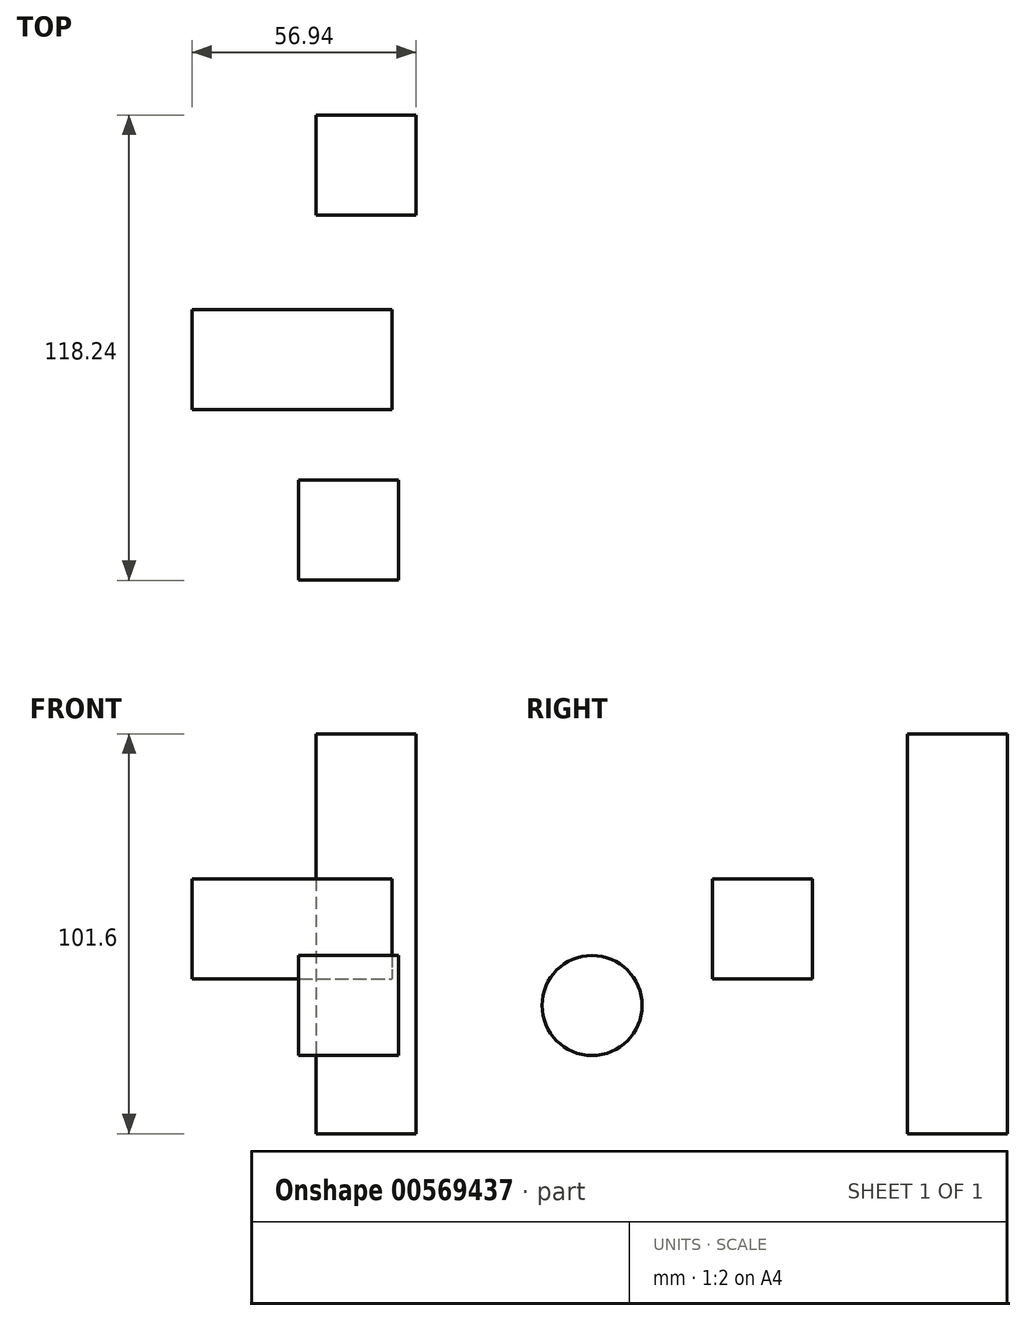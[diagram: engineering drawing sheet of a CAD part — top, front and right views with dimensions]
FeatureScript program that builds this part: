
annotation { "Feature Type Name" : "Feature", "Feature Type Description" : "" }
export const myFeature = defineFeature(function(context is Context, id is Id, definition is map)
    precondition{}
    {
        {
            var Q0;
            Q0=qCreatedBy(makeId("Front.planeOp"),FACE);
            var sketch = newSketch(context, id + "F0", { "sketchPlane" : qUnion([Q0])});
            skLineSegment(sketch, "E0.bottom", {"start": v(-27.11, 64.72) * mm, "end": v(23.69, 64.72) * mm});
            skLineSegment(sketch, "E0.top", {"start": v(-27.11, 39.32) * mm, "end": v(23.69, 39.32) * mm});
            skLineSegment(sketch, "E0.left", {"start": v(-27.11, 64.72) * mm, "end": v(-27.11, 39.32) * mm});
            skLineSegment(sketch, "E0.right", {"start": v(23.69, 64.72) * mm, "end": v(23.69, 39.32) * mm});
            skSolve(sketch);
        }
        {
            var Q0;
            Q0 = qSketchRegion(id + "F0", true);
            extrude(context, id + "F1", {"entities" : qUnion([Q0]), "depth" : 25.4 * mm, "offsetDistance" : 25.4 * mm});
        }
        {
            var Q0;
            Q0=qCreatedBy(makeId("Top.planeOp"),FACE);
            var sketch = newSketch(context, id + "F2", { "sketchPlane" : qUnion([Q0])});
            skLineSegment(sketch, "E1.bottom", {"start": v(29.83, 49.49) * mm, "end": v(4.43, 49.49) * mm});
            skLineSegment(sketch, "E1.top", {"start": v(29.83, 24.09) * mm, "end": v(4.43, 24.09) * mm});
            skLineSegment(sketch, "E1.left", {"start": v(29.83, 49.49) * mm, "end": v(29.83, 24.09) * mm});
            skLineSegment(sketch, "E1.right", {"start": v(4.43, 49.49) * mm, "end": v(4.43, 24.09) * mm});
            skSolve(sketch);
        }
        {
            var Q0;
            Q0=makeQuery(id+"F2.imprint","IMPRINT",FACE,{"disambiguationData":[TD([[makeQuery(id+"F2.imprint","IMPRINT",EDGE,{"derivedFrom":sQuery(id+"F2.wireOp",EDGE,"E1.bottom")}),1.0]])]});
            extrude(context, id + "F3", {"entities" : qUnion([Q0]), "depth" : 101.6 * mm, "offsetDistance" : 25.4 * mm});
        }
        {
            var Q0;
            Q0=qCreatedBy(makeId("Right.planeOp"),FACE);
            var sketch = newSketch(context, id + "F4", { "sketchPlane" : qUnion([Q0])});
            skCircle(sketch, "E2", {"center": v(-56.05, 32.57) * mm, "radius": 12.7 * mm});
            skSolve(sketch);
        }
        {
            var Q0;
            Q0 = qSketchRegion(id + "F4", true);
            extrude(context, id + "F5", {"entities" : qUnion([Q0]), "depth" : 25.4 * mm, "offsetDistance" : 25.4 * mm});
        }
        {
            var Q0;
            Q0 = qSketchRegion(id + "F4", true);
            extrude(context, id + "F6", {"entities" : qUnion([Q0]), "operationType" : NewBodyOperationType.ADD, "depth" : 25.4 * mm, "offsetDistance" : 25.4 * mm});
        }
    });
